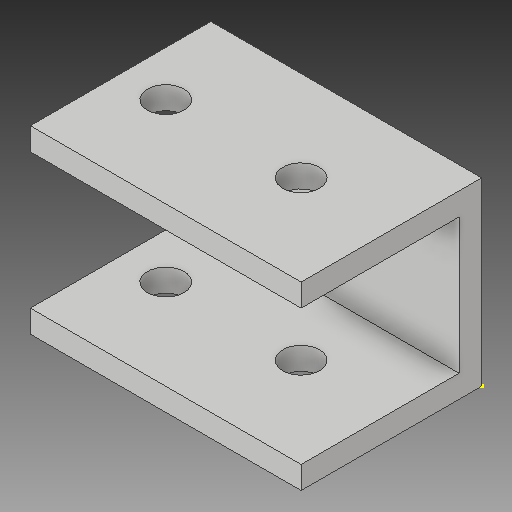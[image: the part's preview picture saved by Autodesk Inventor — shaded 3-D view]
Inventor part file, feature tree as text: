
AUTODESK INVENTOR PART (.ipt)
format: ipt  version: 2018 (Build 220112000, 112)  size: 123,392 bytes
history: native  units: in
note: dims shown in document units (in); Inventor stores cm internally (conversion verified against a paired STEP export)
features: sketch x4, other x3
ambient origin geometry x8: Origin, YZ Plane, XZ Plane, XY Plane, X Axis, Y Axis, Z Axis, Center Point
bodies: Solid1 (feature_tree)
feature tree (7):
  other  "wheel tip connector 1.ipt"
  other  "Solid1::wheel tip connector 1.ipt"
  other  "TaggingFeature1"
  sketch  "Sketch1"  dims[d0=0.3937in]
  sketch  "Sketch2"
  sketch  "Sketch3"
  sketch  "Sketch4"
